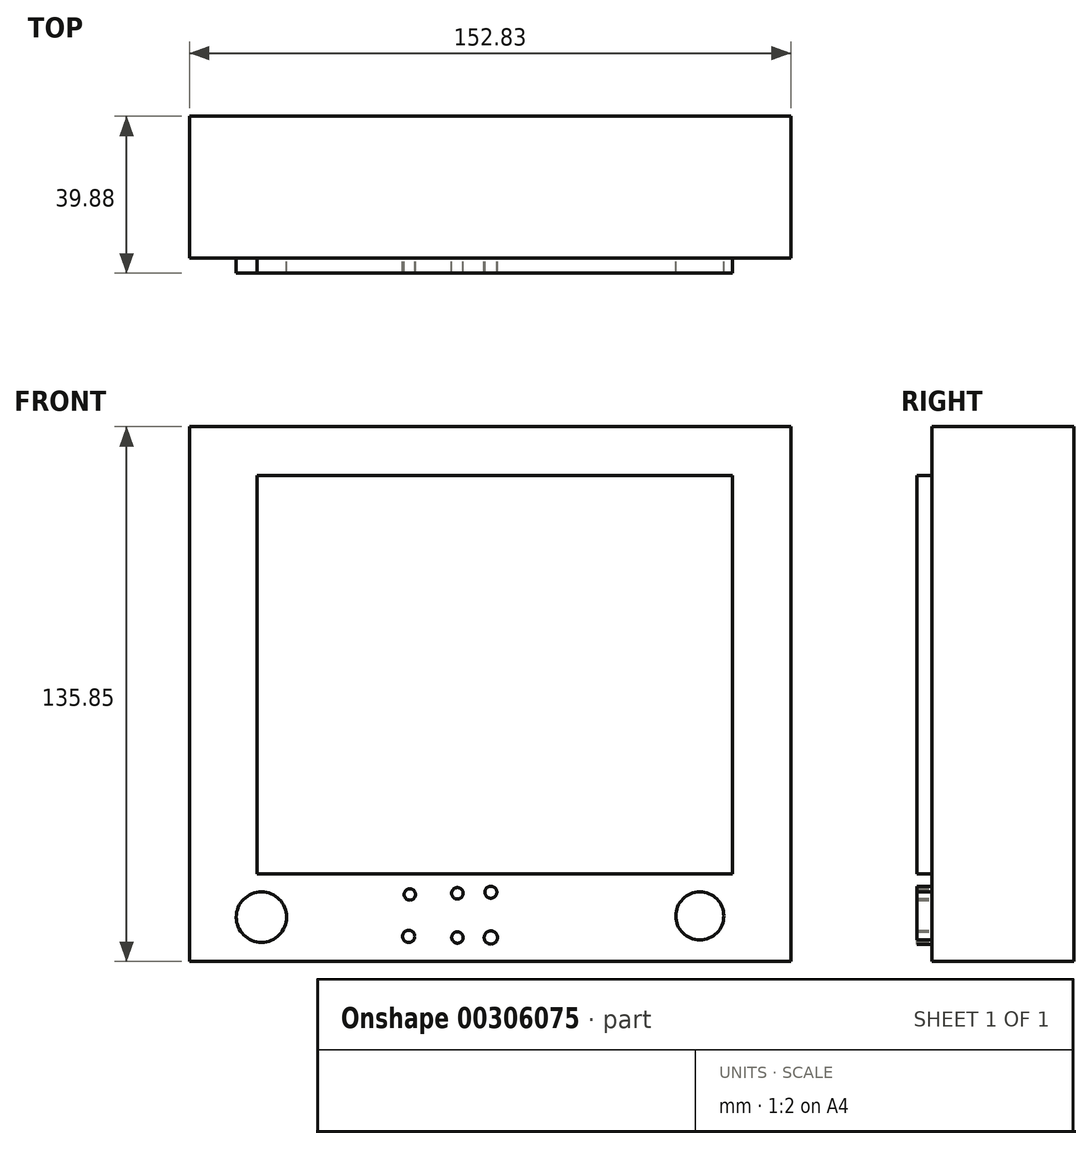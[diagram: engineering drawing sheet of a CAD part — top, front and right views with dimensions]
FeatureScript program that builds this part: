
annotation { "Feature Type Name" : "Feature", "Feature Type Description" : "" }
export const myFeature = defineFeature(function(context is Context, id is Id, definition is map)
    precondition{}
    {
        {
            var Q0;
            Q0=qCreatedBy(makeId("Front.planeOp"),FACE);
            var sketch = newSketch(context, id + "F0", { "sketchPlane" : qUnion([Q0])});
            skLineSegment(sketch, "E0", {"start": v(-76.56, 60.44) * mm, "end": v(-76.56, -75.4) * mm});
            skLineSegment(sketch, "E1", {"start": v(-76.56, -75.4) * mm, "end": v(76.27, -75.4) * mm});
            skLineSegment(sketch, "E2", {"start": v(76.27, -75.4) * mm, "end": v(76.27, 60.44) * mm});
            skLineSegment(sketch, "E3", {"start": v(76.27, 60.44) * mm, "end": v(-76.56, 60.44) * mm});
            skSolve(sketch);
        }
        {
            var Q0;
            Q0 = qSketchRegion(id + "F0", true);
            extrude(context, id + "F1", {"entities" : qUnion([Q0]), "depth" : 36.07 * mm});
        }
        {
            var Q0;
            Q0=makeQuery(id+"F1.opExtrude","CAP_FACE",FACE,{"disambiguationData":[OSD([sQuery(id+"F0.wireOp",EDGE,"E0"),sQuery(id+"F0.wireOp",EDGE,"E1"),sQuery(id+"F0.wireOp",EDGE,"E2"),sQuery(id+"F0.wireOp",EDGE,"E3")])],"isStart":false});
            var sketch = newSketch(context, id + "F2", { "sketchPlane" : qUnion([Q0])});
            skLineSegment(sketch, "E4", {"start": v(-59.43, 48.06) * mm, "end": v(-59.43, -53.24) * mm});
            skLineSegment(sketch, "E5", {"start": v(-59.43, -53.24) * mm, "end": v(61.45, -53.24) * mm});
            skLineSegment(sketch, "E6", {"start": v(61.45, -53.24) * mm, "end": v(61.45, 48.06) * mm});
            skLineSegment(sketch, "E7", {"start": v(61.45, 48.06) * mm, "end": v(-59.43, 48.06) * mm});
            skCircle(sketch, "E8", {"center": v(-58.28, -64.18) * mm, "radius": 6.4 * mm});
            skCircle(sketch, "E9", {"center": v(53.1, -63.9) * mm, "radius": 6.1 * mm});
            skCircle(sketch, "E10", {"center": v(-20.58, -58.42) * mm, "radius": 1.44 * mm});
            skCircle(sketch, "E11", {"center": v(-20.87, -69.07) * mm, "radius": 1.55 * mm});
            skCircle(sketch, "E12", {"center": v(-8.5, -69.36) * mm, "radius": 1.44 * mm});
            skCircle(sketch, "E13", {"center": v(-8.5, -58.14) * mm, "radius": 1.47 * mm});
            skCircle(sketch, "E14", {"center": v(0, -57.85) * mm, "radius": 1.53 * mm});
            skCircle(sketch, "E15", {"center": v(0, -69.36) * mm, "radius": 1.68 * mm});
            skLineSegment(sketch, "E16", {"start": v(-20.58, -58.42) * mm, "end": v(-20.87, -69.07) * mm});
            skLineSegment(sketch, "E17", {"start": v(-8.5, -58.14) * mm, "end": v(-8.5, -69.36) * mm});
            skLineSegment(sketch, "E18", {"start": v(0, -57.85) * mm, "end": v(0, -69.36) * mm});
            skSolve(sketch);
        }
        {
            var Q0;
            Q0 = qSketchRegion(id + "F2", true);
            extrude(context, id + "F3", {"entities" : qUnion([Q0]), "operationType" : NewBodyOperationType.ADD, "depth" : 3.8 * mm});
        }
    });
